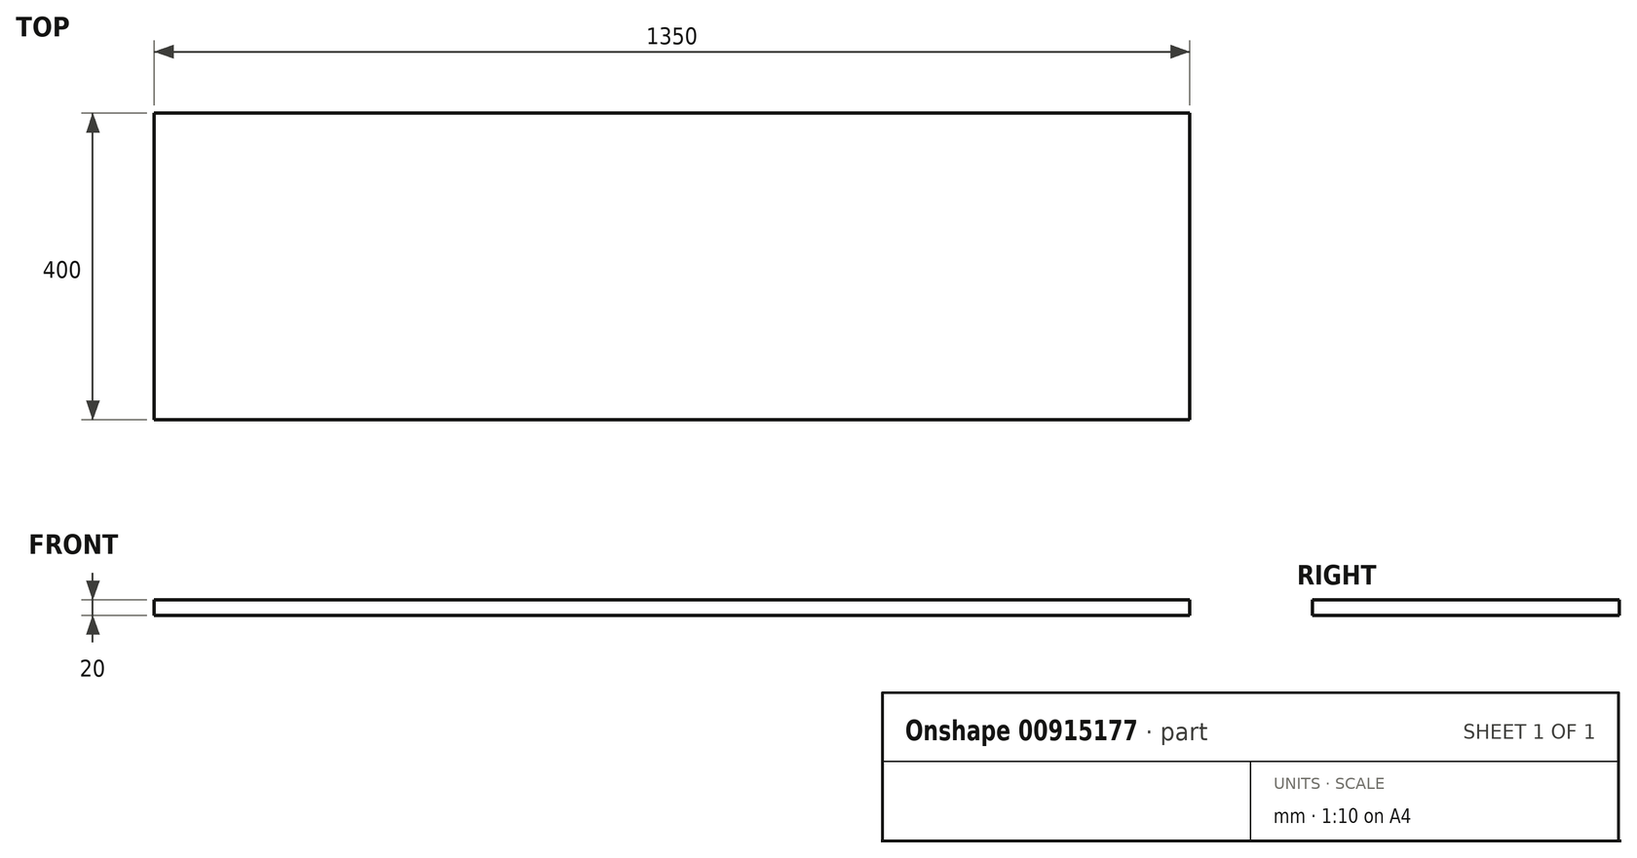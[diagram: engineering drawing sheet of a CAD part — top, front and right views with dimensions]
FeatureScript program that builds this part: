
annotation { "Feature Type Name" : "Feature", "Feature Type Description" : "" }
export const myFeature = defineFeature(function(context is Context, id is Id, definition is map)
    precondition{}
    {
        {
            var Q0;
            Q0=qCreatedBy(makeId("Front.planeOp"),FACE);
            var sketch = newSketch(context, id + "F0", { "sketchPlane" : qUnion([Q0])});
            skLineSegment(sketch, "E0", {"start": v(-74.19, 0) * mm, "end": v(1275.81, 0) * mm});
            skLineSegment(sketch, "E1", {"start": v(1275.81, 0) * mm, "end": v(1275.81, 20) * mm});
            skLineSegment(sketch, "E2", {"start": v(1275.81, 20) * mm, "end": v(-74.19, 20) * mm});
            skLineSegment(sketch, "E3", {"start": v(-74.19, 20) * mm, "end": v(-74.19, 0) * mm});
            skSolve(sketch);
        }
        {
            var Q0;
            Q0 = qSketchRegion(id + "F0", true);
            extrude(context, id + "F1", {"entities" : qUnion([Q0]), "depth" : 400 * mm, "offsetDistance" : 25 * mm});
        }
    });
